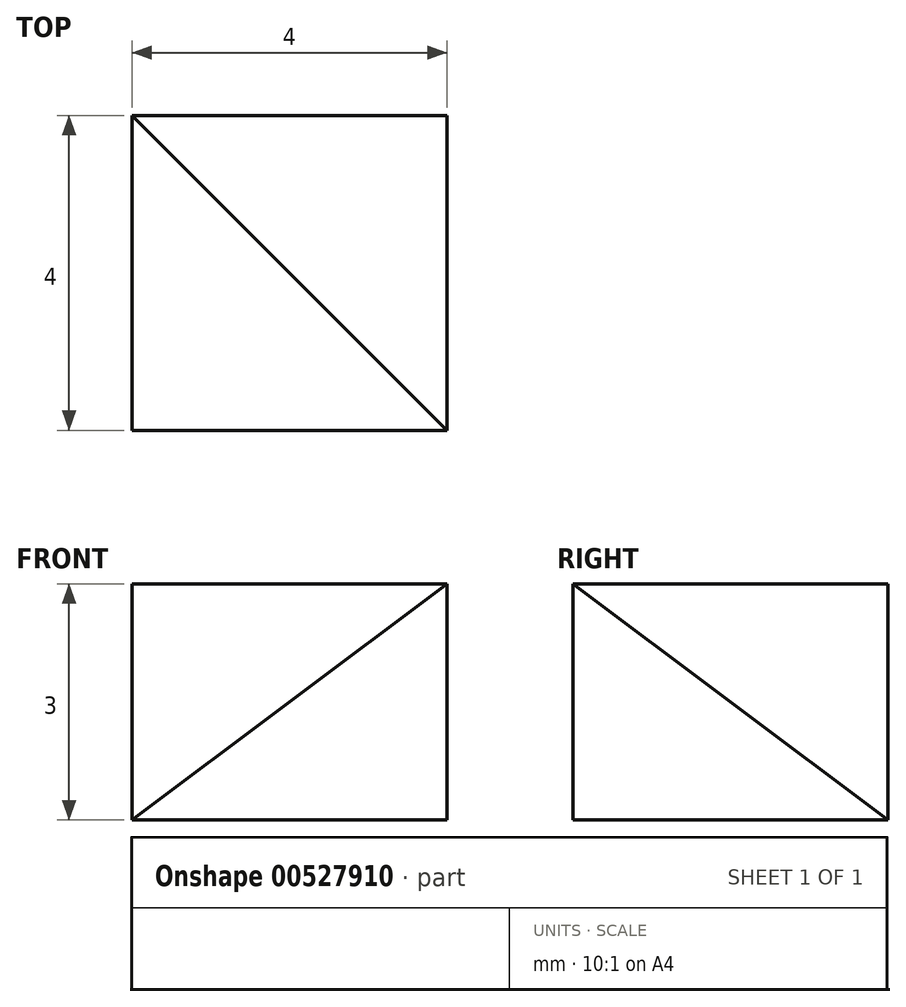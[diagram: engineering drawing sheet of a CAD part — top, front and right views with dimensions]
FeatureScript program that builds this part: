
annotation { "Feature Type Name" : "Feature", "Feature Type Description" : "" }
export const myFeature = defineFeature(function(context is Context, id is Id, definition is map)
    precondition{}
    {
        {
            var Q0;
            Q0=qCreatedBy(makeId("Top.planeOp"),FACE);
            var sketch = newSketch(context, id + "F0", { "sketchPlane" : qUnion([Q0])});
            skLineSegment(sketch, "E0.bottom", {"start": v(0, 0) * mm, "end": v(4, 0) * mm});
            skLineSegment(sketch, "E0.top", {"start": v(0, 4) * mm, "end": v(4, 4) * mm});
            skLineSegment(sketch, "E0.left", {"start": v(0, 0) * mm, "end": v(0, 4) * mm});
            skLineSegment(sketch, "E0.right", {"start": v(4, 0) * mm, "end": v(4, 4) * mm});
            skSolve(sketch);
        }
        {
            var Q0;
            Q0=qSketchRegion(id+"F0",true);
            extrude(context, id + "F1", {"entities" : qUnion([Q0]), "depth" : 3 * mm});
        }
        {
            var Q0;
            Q0=qCreatedBy(makeId("Origin.pointOp"),VERTEX);
            var Q1;
            Q1=makeQuery(id+"F1.opExtrude","CAP_VERTEX",VERTEX,{"disambiguationData":[OSD([sQuery(id+"F0.wireOp",EDGE,"E0.top"),sQuery(id+"F0.wireOp",EDGE,"E0.left")])],"isStart":false});
            var Q2;
            Q2=makeQuery(id+"F1.opExtrude","CAP_VERTEX",VERTEX,{"disambiguationData":[OSD([sQuery(id+"F0.wireOp",EDGE,"E0.bottom"),sQuery(id+"F0.wireOp",EDGE,"E0.right")])],"isStart":false});
            cPlane(context, id + "F2", {"entities" : qUnion([Q0, Q1, Q2]), "cplaneType" : CPlaneType.THREE_POINT, "offset" : 25 * mm, "width" : 150 * mm, "height" : 150 * mm});
        }
        {
            var Q0;
            Q0=qCreatedBy(id+"F2.planeOp",FACE);
            var sketch = newSketch(context, id + "F3", { "sketchPlane" : qUnion([Q0])});
            skPoint(sketch, "E1.0", {"position": v(0, 0) * mm});
            skPoint(sketch, "E1.1", {"position": v(4.66, 1.8) * mm});
            skPoint(sketch, "E1.2", {"position": v(0, 5) * mm});
            skLineSegment(sketch, "E2", {"start": v(0, 0) * mm, "end": v(4.66, 1.8) * mm});
            skLineSegment(sketch, "E3", {"start": v(0, 5) * mm, "end": v(4.66, 1.8) * mm});
            skLineSegment(sketch, "E4", {"start": v(0, 5) * mm, "end": v(0, 0) * mm});
            skSolve(sketch);
        }
        {
            var Q0;
            Q0=qSketchRegion(id+"F3",true);
            extrude(context, id + "F4", {"entities" : qUnion([Q0]), "operationType" : NewBodyOperationType.REMOVE, "depth" : 25 * mm});
        }
        {
            var Q0;
            Q0=makeQuery(id+"F4.boolean.opBoolean","MERGE",VERTEX,{"derivedFrom":[makeQuery(id+"F1.opExtrude","CAP_VERTEX",VERTEX,{"disambiguationData":[OSD([sQuery(id+"F0.wireOp",EDGE,"E0.bottom"),sQuery(id+"F0.wireOp",EDGE,"E0.right")])],"isStart":false}),makeQuery(id+"F4.opExtrude","CAP_VERTEX",VERTEX,{"disambiguationData":[OSD([sQuery(id+"F3.wireOp",EDGE,"E2"),sQuery(id+"F3.wireOp",EDGE,"E3")])],"isStart":true})]});
            var Q1;
            Q1=makeQuery(id+"F1.opExtrude","CAP_VERTEX",VERTEX,{"disambiguationData":[OSD([sQuery(id+"F0.wireOp",EDGE,"E0.top"),sQuery(id+"F0.wireOp",EDGE,"E0.right")])],"isStart":true});
            var Q2;
            Q2=makeQuery(id+"F4.boolean.opBoolean","MERGE",VERTEX,{"derivedFrom":[makeQuery(id+"F1.opExtrude","CAP_VERTEX",VERTEX,{"disambiguationData":[OSD([sQuery(id+"F0.wireOp",EDGE,"E0.top"),sQuery(id+"F0.wireOp",EDGE,"E0.left")])],"isStart":false}),makeQuery(id+"F4.opExtrude","CAP_VERTEX",VERTEX,{"disambiguationData":[OSD([sQuery(id+"F3.wireOp",EDGE,"E3"),sQuery(id+"F3.wireOp",EDGE,"E4")])],"isStart":true})]});
            cPlane(context, id + "F5", {"entities" : qUnion([Q0, Q1, Q2]), "cplaneType" : CPlaneType.THREE_POINT, "offset" : 25 * mm, "width" : 150 * mm, "height" : 150 * mm});
        }
        {
            var Q0;
            Q0=qCreatedBy(id+"F5.planeOp",FACE);
            var sketch = newSketch(context, id + "F6", { "sketchPlane" : qUnion([Q0])});
            skPoint(sketch, "E5.0", {"position": v(2.2, 1.8) * mm});
            skPoint(sketch, "E5.1", {"position": v(2.2, -3.2) * mm});
            skPoint(sketch, "E5.2", {"position": v(-2.47, -1.4) * mm});
            skLineSegment(sketch, "E6", {"start": v(2.2, 1.8) * mm, "end": v(-2.47, -1.4) * mm});
            skLineSegment(sketch, "E7", {"start": v(-2.47, -1.4) * mm, "end": v(2.2, -3.2) * mm});
            skLineSegment(sketch, "E8", {"start": v(2.2, -3.2) * mm, "end": v(2.2, 1.8) * mm});
            skSolve(sketch);
        }
        {
            var Q0;
            Q0=qSketchRegion(id+"F6",true);
            extrude(context, id + "F7", {"entities" : qUnion([Q0]), "operationType" : NewBodyOperationType.REMOVE, "oppositeDirection" : true, "depth" : 25 * mm});
        }
    });
